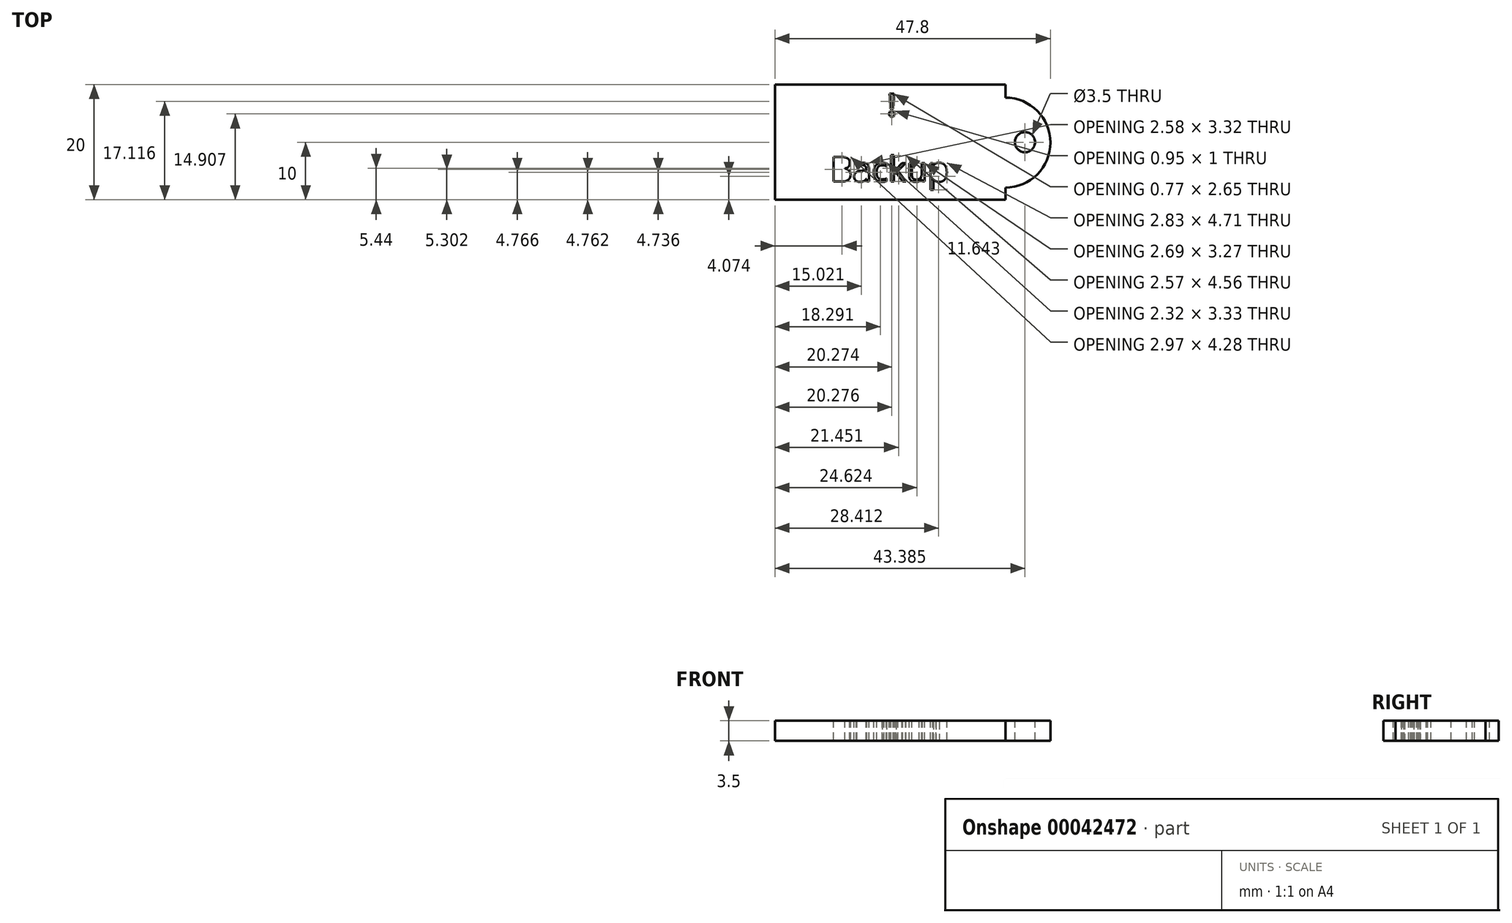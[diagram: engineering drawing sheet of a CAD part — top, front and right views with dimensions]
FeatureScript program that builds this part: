
annotation { "Feature Type Name" : "Feature", "Feature Type Description" : "" }
export const myFeature = defineFeature(function(context is Context, id is Id, definition is map)
    precondition{}
    {
        {
            var Q0;
            Q0=qCreatedBy(makeId("Top.planeOp"),FACE);
            var sketch = newSketch(context, id + "F1", { "sketchPlane" : qUnion([Q0])});
            skLineSegment(sketch, "E0.rect.bottom", {"start": v(20, 10) * mm, "end": v(-20, 10) * mm});
            skLineSegment(sketch, "E0.rect.top", {"start": v(20, -10) * mm, "end": v(-20, -10) * mm});
            skLineSegment(sketch, "E0.rect.left", {"start": v(20, 10) * mm, "end": v(20, -10) * mm});
            skLineSegment(sketch, "E0.rect.right", {"start": v(-20, 10) * mm, "end": v(-20, -10) * mm});
            skPoint(sketch, "E0.rect.middle", {"position": v(0, 0) * mm});
            skArc(sketch, "E1", {"start": v(20, -7.88) * mm, "mid": v(27.8, -0.07) * mm, "end": v(20, 7.73) * mm});
            skCircle(sketch, "E2", {"center": v(23.39, 0) * mm, "radius": 1.75 * mm});
            skText(sketch, "E3", { "text": "Backup", "fontName": "OpenSans-Regular.ttf"});
            skText(sketch, "E4", { "text": "!", "fontName": "NotoSansCJKsc-Bold.otf"});
            const initialGuessFZEyUgFY3KBtZn3j2_0  = {"E3": [-0.01043, -0.00684, 1, 0, 0.00432], "E4": [-0.00069, 0.00448, 1, 0, 0.00375]};
            skSetInitialGuess(sketch, initialGuessFZEyUgFY3KBtZn3j2_0);
            skSolve(sketch);
        }
        {
            var Q0;
            {var subQ4=sQuery(id+"F1.wireOp",EDGE,"E0.rect.bottom");Q0=makeQuery(id+"F1.imprint","IMPRINT",FACE,{"disambiguationData":[TD([[makeQuery(id+"F1.imprint","IMPRINT",EDGE,{"derivedFrom":subQ4}),1.0]])]});}
            var Q1;
            {var subQ0=sQuery(id+"F1.wireOp",EDGE,"E1");Q1=makeQuery(id+"F1.imprint","IMPRINT",FACE,{"disambiguationData":[TD([[makeQuery(id+"F1.imprint","IMPRINT",EDGE,{"derivedFrom":subQ0}),1.0]])]});}
            extrude(context, id + "F0", {"entities" : qUnion([Q0, Q1]), "oppositeDirection" : true, "depth" : 3.5 * mm});
        }
    });
